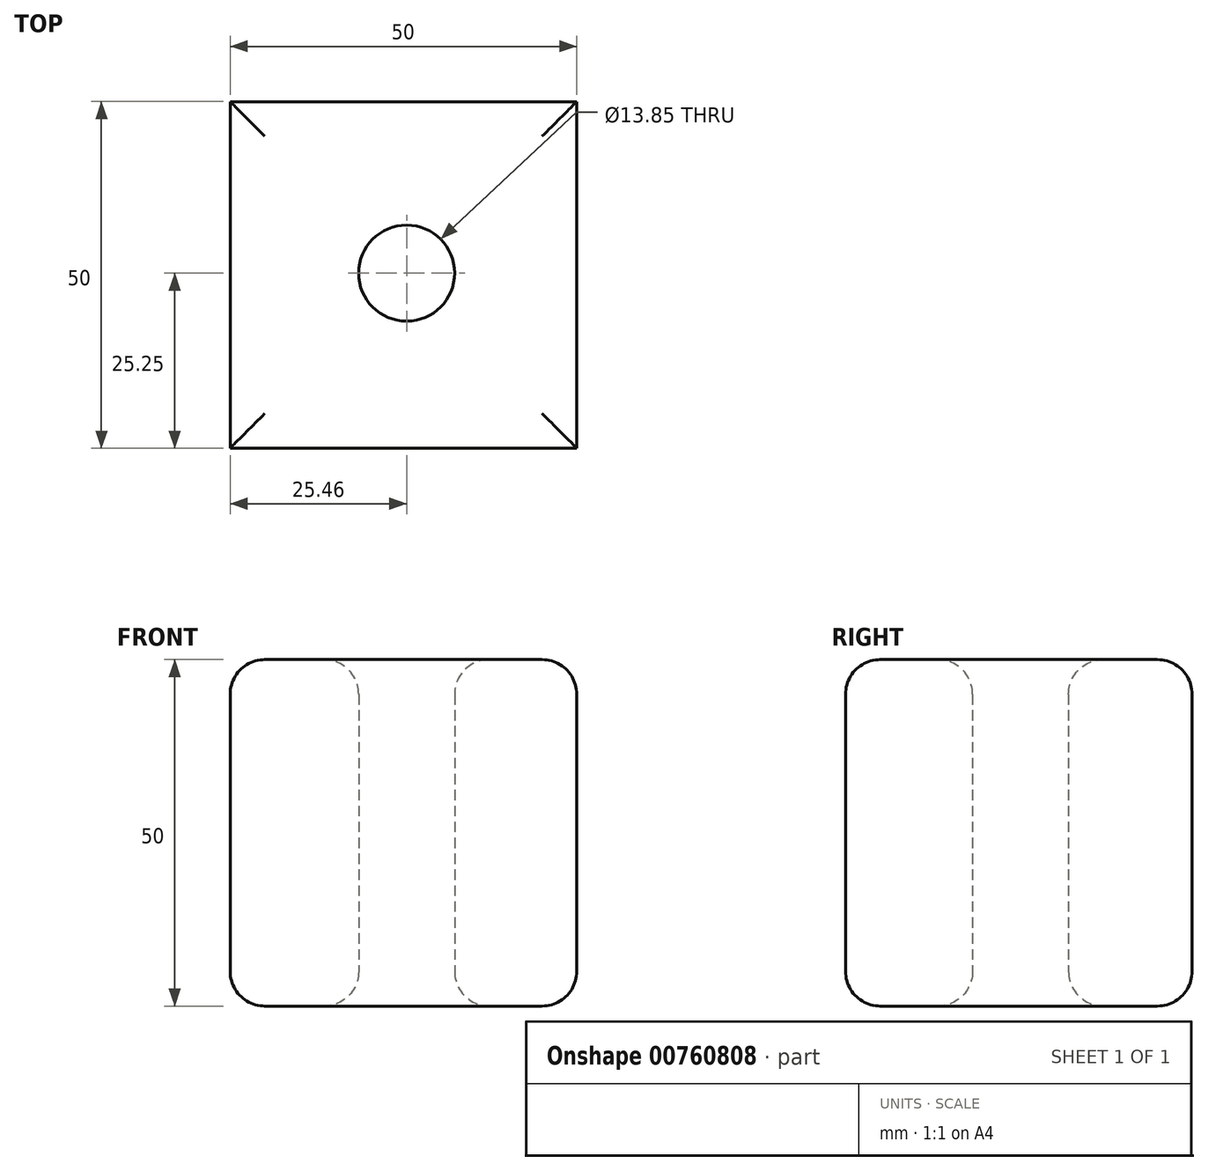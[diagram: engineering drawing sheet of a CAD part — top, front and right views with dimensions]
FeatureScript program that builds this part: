
annotation { "Feature Type Name" : "Feature", "Feature Type Description" : "" }
export const myFeature = defineFeature(function(context is Context, id is Id, definition is map)
    precondition{}
    {
        {
            var Q0;
            Q0=qCreatedBy(makeId("Top.planeOp"),FACE);
            var sketch = newSketch(context, id + "F0", { "sketchPlane" : qUnion([Q0])});
            skLineSegment(sketch, "E0.bottom", {"start": v(-25.46, 24.75) * mm, "end": v(24.54, 24.75) * mm});
            skLineSegment(sketch, "E0.top", {"start": v(-25.46, -25.25) * mm, "end": v(24.54, -25.25) * mm});
            skLineSegment(sketch, "E0.left", {"start": v(-25.46, 24.75) * mm, "end": v(-25.46, -25.25) * mm});
            skLineSegment(sketch, "E0.right", {"start": v(24.54, 24.75) * mm, "end": v(24.54, -25.25) * mm});
            skCircle(sketch, "E1", {"center": v(0, 0) * mm, "radius": 6.93 * mm});
            skSolve(sketch);
        }
        {
            var Q0;
            Q0 = qSketchRegion(id + "F0", true);
            extrude(context, id + "F1", {"entities" : qUnion([Q0]), "depth" : 50 * mm, "offsetDistance" : 25 * mm});
        }
        {
            var Q0;
            Q0 = qSketchRegion(id + "F0", true);
            extrude(context, id + "F2", {"entities" : qUnion([Q0]), "operationType" : NewBodyOperationType.REMOVE, "oppositeDirection" : true, "depth" : 20 * mm, "offsetDistance" : 25 * mm});
        }
        {
            var Q0;
            Q0=makeQuery(id+"F1.opExtrude","CAP_FACE",FACE,{"disambiguationData":[OSD([sQuery(id+"F0.wireOp",EDGE,"E0.bottom"),sQuery(id+"F0.wireOp",EDGE,"E0.top"),sQuery(id+"F0.wireOp",EDGE,"E0.left"),sQuery(id+"F0.wireOp",EDGE,"E0.right"),sQuery(id+"F0.wireOp",EDGE,"E1")])],"isStart":false});
            fillet(context, id + "F3", {"entities" : qUnion([Q0]), "radius" : 5 * mm, "tangentPropagation" : true, "allowEdgeOverflow" : false});
        }
        {
            var Q0;
            Q0=makeQuery(id+"F1.opExtrude","CAP_FACE",FACE,{"disambiguationData":[OSD([sQuery(id+"F0.wireOp",EDGE,"E0.bottom"),sQuery(id+"F0.wireOp",EDGE,"E0.top"),sQuery(id+"F0.wireOp",EDGE,"E0.left"),sQuery(id+"F0.wireOp",EDGE,"E0.right"),sQuery(id+"F0.wireOp",EDGE,"E1")])],"isStart":true});
            fillet(context, id + "F4", {"entities" : qUnion([Q0]), "radius" : 5 * mm, "tangentPropagation" : true, "allowEdgeOverflow" : false});
        }
    });
